# Revit family: Haworth_Masters_OpenSidedShelf_TwoHigh
name_source: partatom
category: Furniture Systems
revit_build: Autodesk Revit 2018 (Build: 20170223_1515(x64)
units: mm (PartAtom-declared; Revit-internal decimal feet)

## family parameters
Always vertical = Yes
Cut with Voids When Loaded = No
OmniClass Number = 23.40.70.14.64.21
OmniClass Title = Systems Furniture
Part Type = Normal
Room Calculation Point = No
Round Connector Dimension = Use Diameter
Shared = No
Work Plane-Based = No

## types (4) — shared parameters
Assembly Code = E2020500
Custom Size = No
Legal Depth = No
Letter Depth = Yes
Manufacturer = Haworth
Max. Width = 120"
Min. Width = 30"
Min/Max Height = 17 in. Single Shelf or 29 in. Double Shelf
Min/Max Width = 30-120 in. @ 6 in. Increments
Model = Masters Series
Panel Depth = 3/4"
Revision Number = 1
Shelf Depth = 14"
Size = Verify Final Dim. w/ Haworth
Sustainability Info = http://media.haworth.com
URL = http://www.haworth.com
URL - Product = http://www.haworth.com
Warranty = http://www.haworth.com

## per-type parameters (varying)
| type | Actual Height | Actual Width | Description | One High | Two High | Width |
| 30w - One High - Letter Depth | 17" | 30" | Masters Series Open Ended Shelving - One High Letter Depth | Yes | No | 30" |
| 30w - Two High - Letter Depth | 29" | 30" | Masters Series Open Ended Shelving | No | Yes | 30" |
| 42w - One High - Letter Depth | 17" | 42" | Masters Series Open Ended Shelving | Yes | No | 42" |
| 42w - Two High - Letter Depth | 29" | 42" | Masters Series Open Ended Shelving | No | Yes | 42" |

## geometry (parser evidence)
native form markers: Sweep x2
no freeform markers — native parametric forms only
